# Revit family: CENTUM Konsole XL 80
name_source: partatom
category: HLS-Bauteile
revit_build: Autodesk Revit 2017 (Build: 20190508_0315(x64)
units: mm (PartAtom-declared; Revit-internal decimal feet)

## family parameters
Basisbauteil = Fläche
Beim Laden mit Abzugskörper schneiden = Nein
Bemaßung runder Anschluss = Durchmesser verwenden
Gemeinsam genutzt = Ja
Raumberechnungspunkt = Nein
Teiletyp = Normal

## types (3) — shared parameters
Breite Platte = 220 mm
Breite Profil = 80 mm  [stored 0.262467 ft]
Fabrikat = MEFA
Firma = MEFA Befestigungs- und Montagesysteme GmbH
Höhe Profil = 80 mm  [stored 0.262467 ft]
Kurztext1 = Konsole Centum XL 80
Langloch Platte = 27x14 mm
Lochabstand = 150 mm
Länge Platte = 220 mm
Material = Stahl
Materialname C-Profil = S235JR
Materialname Platte = S235JR
Oberflaeche = feuerstückverzinkt
Profil = CENTUM
Stärke Platte = 15 mm  [stored 0.0492126 ft]
Stärke Profil = 3 mm  [stored 0.00984252 ft]
Vorgabe-Ansicht = 1219 mm

## per-type parameters (varying)
| type | Artikelnummer | EAN | Gewicht | Gewicht pro Bauteil | Kurztext2 | Länge Konsole | Schienenlänge | max. zul. Last F1 | max. zul. Last F2 | max. zul. Last q0 |
| CENTUM Konsole XL 80 L=1440 | 1630801440 | 4250928450395 | 11.23 kg | 11.23 kg | L= 1.440 mm fsv | 1 mm  [stored 0.00328084 ft] | CENTUM Profil XL 80 für Konsole_ : CENTUM Profil XL 80 L=1440 | 0.94 kip | 0.42 kip | 0.286 kip/ft |
| CENTUM Konsole XL 80 L= 960 | 1630800960 | 4250928450388 | 8.58 kg | 8.58 kg | L= 960 mm fsv | 960 mm  [stored 3.14961 ft] | CENTUM Profil XL 80 für Konsole_ : CENTUM Profil XL 80 L= 960 | 1.41 kip | 0.66 kip | 0.449 kip/ft |
| CENTUM Konsole XL 80 L= 720 | 1630800720 | 4250928458438 | 7.26 kg | 7.26 kg | L= 720 mm fsv | 720 mm  [stored 2.3622 ft] | CENTUM Profil XL 80 für Konsole_ : CENTUM Profil XL 80 L= 720 | 1.88 kip | 0.94 kip | 0.798 kip/ft |

note: [stored X ft] marks values corroborated as IEEE doubles in the binary element streams (Revit-internal decimal feet)
